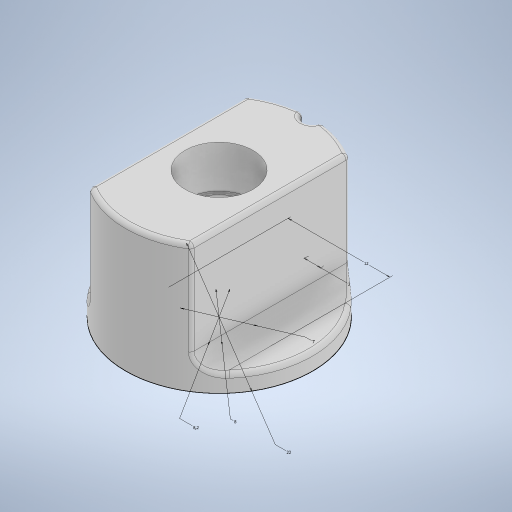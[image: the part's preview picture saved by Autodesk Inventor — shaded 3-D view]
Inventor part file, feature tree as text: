
AUTODESK INVENTOR PART (.ipt)
format: ipt  version: 2024 (Build 280153000, 153)  size: 393,216 bytes
history: native  units: mm
features: extrude x6, fillet x3, other x1, sketch x1
ambient origin geometry x8: Origin, YZ Plane, XZ Plane, XY Plane, X Axis, Y Axis, Z Axis, Center Point
bodies: Body1 (feature_tree)
feature tree (11):
  other  "Твердое тело1"
  sketch  "Эскиз1"
  extrude  "Выдавливание1"  Depth=6.15mm
  extrude  "Выдавливание2"  Depth=8.0mm
  fillet  "Сопряжение3"  Radius=22.0mm
  fillet  "Сопряжение7"  Radius=12.0mm
  extrude  "Выдавливание10"  Depth=2.0mm
  extrude  "Выдавливание11"  Depth=2.0mm TaperAngle=0.0deg
  extrude  "Выдавливание12"  Depth=15.0mm TaperAngle=0.0deg
  extrude  "Выдавливание13"  Depth=2.0mm
  fillet  "Сопряжение14"  Radius=7.0mm
